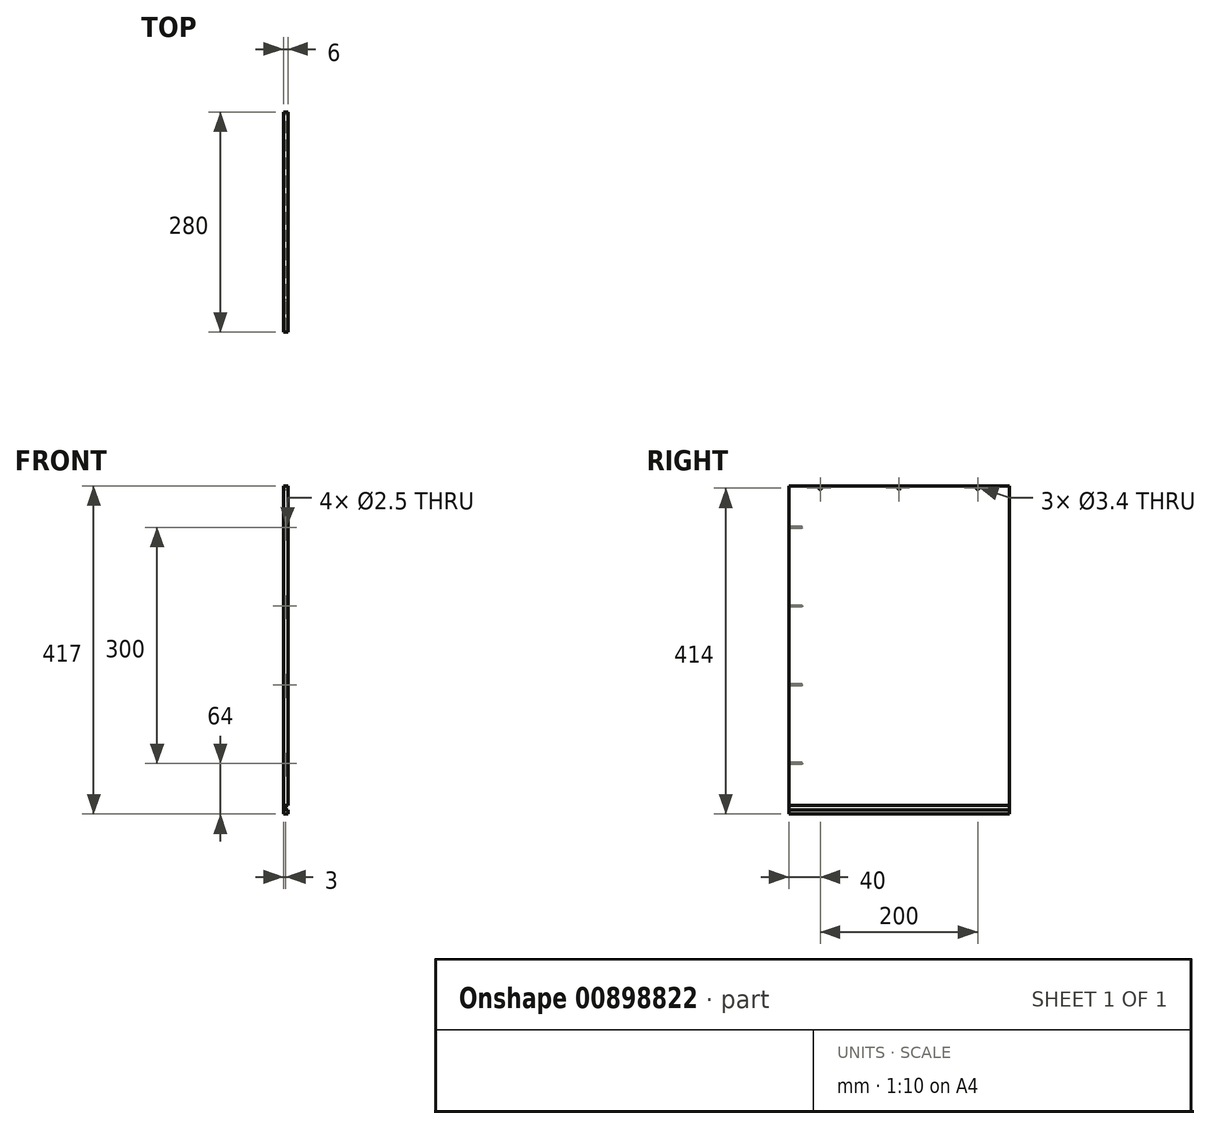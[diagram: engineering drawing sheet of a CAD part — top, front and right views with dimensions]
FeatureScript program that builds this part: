
annotation { "Feature Type Name" : "Feature", "Feature Type Description" : "" }
export const myFeature = defineFeature(function(context is Context, id is Id, definition is map)
    precondition{}
    {
        {
            var Q0;
            Q0=qCreatedBy(makeId("Right.planeOp"),FACE);
            var sketch = newSketch(context, id + "F0", { "sketchPlane" : qUnion([Q0])});
            skLineSegment(sketch, "E0.bottom", {"start": v(140, 208.5) * mm, "end": v(-140, 208.5) * mm});
            skLineSegment(sketch, "E0.top", {"start": v(140, -208.5) * mm, "end": v(-140, -208.5) * mm});
            skLineSegment(sketch, "E0.left", {"start": v(140, 208.5) * mm, "end": v(140, -208.5) * mm});
            skLineSegment(sketch, "E0.right", {"start": v(-140, 208.5) * mm, "end": v(-140, -208.5) * mm});
            skPoint(sketch, "E0.middle", {"position": v(0, 0) * mm});
            skSolve(sketch);
        }
        {
            var Q0;
            Q0=makeQuery(id+"F0.imprint","IMPRINT",FACE,{"disambiguationData":[TD([[makeQuery(id+"F0.imprint","IMPRINT",EDGE,{"derivedFrom":sQuery(id+"F0.wireOp",EDGE,"E0.bottom")}),1.0]])]});
            extrude(context, id + "F1", {"entities" : qUnion([Q0]), "depth" : 6 * mm, "offsetDistance" : 25 * mm});
        }
        {
            var Q0;
            Q0=makeQuery(id+"F1.opExtrude","CAP_FACE",FACE,{"disambiguationData":[OSD([sQuery(id+"F0.wireOp",EDGE,"E0.bottom"),sQuery(id+"F0.wireOp",EDGE,"E0.top"),sQuery(id+"F0.wireOp",EDGE,"E0.left"),sQuery(id+"F0.wireOp",EDGE,"E0.right")])],"isStart":false});
            var sketch = newSketch(context, id + "F2", { "sketchPlane" : qUnion([Q0])});
            skPoint(sketch, "E1", {"position": v(-100, 205.5) * mm});
            skPoint(sketch, "E2", {"position": v(0, 205.5) * mm});
            skPoint(sketch, "E3", {"position": v(100, 205.5) * mm});
            skSolve(sketch);
        }
        {
            var Q0;
            Q0=sQuery(id+"F2.wireOp",VERTEX,"E3");
            var Q1;
            Q1=sQuery(id+"F2.wireOp",VERTEX,"E2");
            var Q2;
            Q2=sQuery(id+"F2.wireOp",VERTEX,"E1");
            var Q3;
            Q3=makeQuery(id+"F1.opExtrude","SWEPT_BODY",BODY,{"disambiguationData":[OSD([sQuery(id+"F0.wireOp",EDGE,"E0.bottom"),sQuery(id+"F0.wireOp",EDGE,"E0.top"),sQuery(id+"F0.wireOp",EDGE,"E0.left"),sQuery(id+"F0.wireOp",EDGE,"E0.right")])]});
            hole(context, id + "F3", {"style" : HoleStyle.SIMPLE, "endStyle" : HoleEndStyle.THROUGH, "standardTappedOrClearance" : lookupTablePath({ "fit" : "Normal", "standard" : "ISO", "size" : "M3", "type" : "Clearance" }), "standardBlindInLast" : lookupTablePath({ "fit" : "Normal", "standard" : "ISO", "size" : "M3", "type" : "Clearance" }), "holeDiameter" : 3.4 * mm, "majorDiameter" : 3 * mm, "tappedDepth" : 15 * mm, "tapClearance" : 3, "locations" : qUnion([Q0, Q1, Q2]), "scope" : qUnion([Q3])});
        }
        {
            var Q0;
            Q0=makeQuery(id+"F1.opExtrude","CAP_FACE",FACE,{"disambiguationData":[OSD([sQuery(id+"F0.wireOp",EDGE,"E0.bottom"),sQuery(id+"F0.wireOp",EDGE,"E0.top"),sQuery(id+"F0.wireOp",EDGE,"E0.left"),sQuery(id+"F0.wireOp",EDGE,"E0.right")])],"isStart":false});
            var sketch = newSketch(context, id + "F4", { "sketchPlane" : qUnion([Q0])});
            skLineSegment(sketch, "E4.bottom", {"start": v(-140, -197.4) * mm, "end": v(140, -197.4) * mm});
            skLineSegment(sketch, "E4.top", {"start": v(-140, -203.5) * mm, "end": v(140, -203.5) * mm});
            skLineSegment(sketch, "E4.left", {"start": v(-140, -197.4) * mm, "end": v(-140, -203.5) * mm});
            skLineSegment(sketch, "E4.right", {"start": v(140, -197.4) * mm, "end": v(140, -203.5) * mm});
            skSolve(sketch);
        }
        {
            var Q0;
            Q0 = qSketchRegion(id + "F4", true);
            extrude(context, id + "F5", {"entities" : qUnion([Q0]), "oppositeDirection" : true, "depth" : 3 * mm, "offsetDistance" : 25 * mm});
        }
        {
            var Q0;
            Q0=makeQuery(id+"F5.opExtrude","SWEPT_BODY",BODY,{"disambiguationData":[OSD([sQuery(id+"F4.wireOp",EDGE,"E4.bottom"),sQuery(id+"F4.wireOp",EDGE,"E4.top"),sQuery(id+"F4.wireOp",EDGE,"E4.left"),sQuery(id+"F4.wireOp",EDGE,"E4.right")])]});
            var Q1;
            Q1=makeQuery(id+"F1.opExtrude","SWEPT_BODY",BODY,{"disambiguationData":[OSD([sQuery(id+"F0.wireOp",EDGE,"E0.bottom"),sQuery(id+"F0.wireOp",EDGE,"E0.top"),sQuery(id+"F0.wireOp",EDGE,"E0.left"),sQuery(id+"F0.wireOp",EDGE,"E0.right")])]});
            booleanBodies(context, id + "F6", {"operationType" : BooleanOperationType.SUBTRACTION, "tools" : qUnion([Q0]), "targets" : qUnion([Q1])});
        }
        {
            var Q0;
            Q0=makeQuery(id+"F1.opExtrude","SWEPT_FACE",FACE,{"disambiguationData":[OSD([sQuery(id+"F0.wireOp",EDGE,"E0.right")])]});
            var sketch = newSketch(context, id + "F7", { "sketchPlane" : qUnion([Q0])});
            skPoint(sketch, "E5", {"position": v(3, 155.5) * mm});
            skPoint(sketch, "E6", {"position": v(3, 55.5) * mm});
            skPoint(sketch, "E7", {"position": v(3, -44.5) * mm});
            skPoint(sketch, "E8", {"position": v(3, -144.5) * mm});
            skSolve(sketch);
        }
        {
            var Q0;
            Q0=sQuery(id+"F7.wireOp",VERTEX,"E5");
            var Q1;
            Q1=sQuery(id+"F7.wireOp",VERTEX,"E6");
            var Q2;
            Q2=sQuery(id+"F7.wireOp",VERTEX,"E7");
            var Q3;
            Q3=sQuery(id+"F7.wireOp",VERTEX,"8e876009-c5cd-4d39-95bb-190775558dd0");
            var Q4;
            Q4=makeQuery(id+"F1.opExtrude","SWEPT_BODY",BODY,{"disambiguationData":[OSD([sQuery(id+"F0.wireOp",EDGE,"E0.bottom"),sQuery(id+"F0.wireOp",EDGE,"E0.top"),sQuery(id+"F0.wireOp",EDGE,"E0.left"),sQuery(id+"F0.wireOp",EDGE,"E0.right")])]});
            hole(context, id + "F8", {"style" : HoleStyle.SIMPLE, "endStyle" : HoleEndStyle.BLIND, "standardTappedOrClearance" : lookupTablePath({ "standard" : "ISO", "engagement" : "75%", "pitch" : "0.5 mm", "size" : "M3", "type" : "Tapped" }), "standardBlindInLast" : lookupTablePath({ "standard" : "ISO", "engagement" : "75%", "pitch" : "0.5 mm", "size" : "M3", "type" : "Tapped" }), "holeDiameter" : 2.5 * mm, "majorDiameter" : 3 * mm, "showTappedDepth" : true, "holeDepth" : 16.5 * mm, "tappedDepth" : 15 * mm, "tapClearance" : 3, "locations" : qUnion([Q0, Q1, Q2, Q3]), "scope" : qUnion([Q4])});
        }
        {
            var Q0;
            Q0=sQuery(id+"F7.wireOp",VERTEX,"E8");
            var Q1;
            Q1=makeQuery(id+"F1.opExtrude","SWEPT_BODY",BODY,{"disambiguationData":[OSD([sQuery(id+"F0.wireOp",EDGE,"E0.bottom"),sQuery(id+"F0.wireOp",EDGE,"E0.top"),sQuery(id+"F0.wireOp",EDGE,"E0.left"),sQuery(id+"F0.wireOp",EDGE,"E0.right")])]});
            hole(context, id + "F9", {"style" : HoleStyle.SIMPLE, "endStyle" : HoleEndStyle.BLIND, "standardTappedOrClearance" : lookupTablePath({ "standard" : "ISO", "engagement" : "75%", "pitch" : "0.5 mm", "size" : "M3", "type" : "Tapped" }), "standardBlindInLast" : lookupTablePath({ "standard" : "ISO", "fit" : "Normal", "engagement" : "75%", "pitch" : "0.5 mm", "size" : "M3", "type" : "Clearance & tapped" }), "holeDiameter" : 2.5 * mm, "majorDiameter" : 3 * mm, "showTappedDepth" : true, "holeDepth" : 16.5 * mm, "tappedDepth" : 15 * mm, "tapClearance" : 3, "locations" : qUnion([Q0]), "scope" : qUnion([Q1])});
        }
    });
